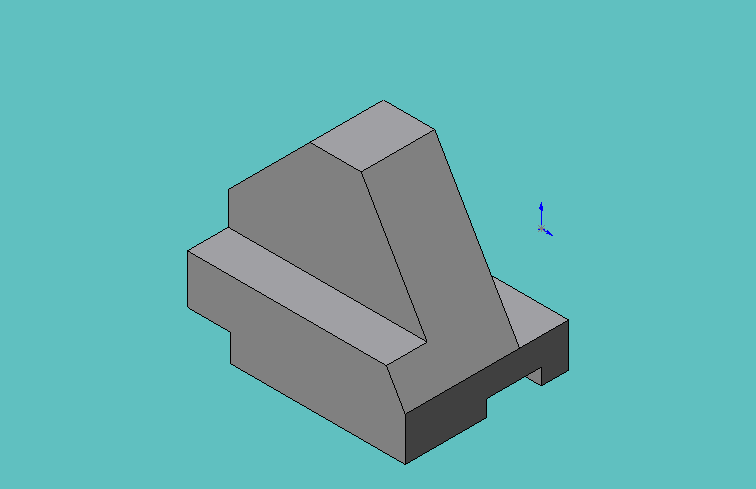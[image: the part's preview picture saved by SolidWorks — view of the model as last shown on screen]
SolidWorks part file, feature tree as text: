
SOLIDWORKS PART (.sldprt)
format: sldprt  version: not decoded by parser v0  size: 153,088 bytes
history: native  units: mm
features: sketch x7, cut_extrude x6, plane x3, material x1, extrude x1 (+7 scaffold rows collapsed)
feature tree (25):
  scaffold x7  (default folders/planes/origin — collapsed)
  material  "Matériau <non spécifié>"
  plane  "Plan1"
  plane  "Plan2"
  plane  "Plan3"
  sketch  "Esquisse1"  dims[D1=80.0mm D2=70.0mm]
  extrude  "Base-Extrusion"  Depth=60mm
  sketch  "Esquisse2"  dims[D1=15.0mm D2=28.0mm]
  cut_extrude  "Enlèv. mat.-Extru.1"  [1 undecoded]
  sketch  "Esquisse3"  dims[D1=18.0mm D2=16.0mm]
  cut_extrude  "Enlèv. mat.-Extru.2"  [1 undecoded]
  sketch  "Esquisse4"  dims[D1=16.0mm D2=10.0mm]
  cut_extrude  "Enlèv. mat.-Extru.3"  [1 undecoded]
  sketch  "Esquisse5"  dims[D1=20.0mm D2=6.0mm D3=30.0mm]
  cut_extrude  "Enlèv. mat.-Extru.4"  [1 undecoded]
  sketch  "Esquisse6"  dims[c1.D1=12.0mm c1.D2=~42.426407mm c2.D2=45.0deg]
  cut_extrude  "Enlèv. mat.-Extru.5"  [1 undecoded]
  sketch  "Esquisse7"  dims[c1.D1=16.0mm c1.D2=~61.773781mm c2.D2=30.0deg]
  cut_extrude  "Enlèv. mat.-Extru.6"  [1 undecoded]
decode coverage: 8 of 14 modeling features carry decoded parameters
note: ~ marks probable driven/reference dimensions
note: 6 parameter values undecoded
summary: no parameter record found for 6 features
note: suppression state not decoded; provenance and decode notes live in map.json
